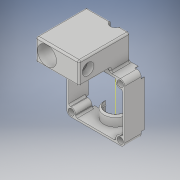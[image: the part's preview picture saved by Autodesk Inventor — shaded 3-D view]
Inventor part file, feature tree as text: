
AUTODESK INVENTOR PART (.ipt)
format: ipt  version: 2018 (Build 220112000, 112)  size: 484,864 bytes
history: native  units: mm
features: sketch x17, extrude x16, fillet x4, pattern_circular x3, mirror x2, other x1, revolve x1, chamfer x1
ambient origin geometry x8: Origin, YZ Plane, XZ Plane, XY Plane, X Axis, Y Axis, Z Axis, Center Point
bodies: Volumenkörper1 (feature_tree)
feature tree (45):
  extrude  "Extrusion1"  Depth=35.3mm
  extrude  "Extrusion2"  Depth=32.8mm
  extrude  "Extrusion3"  Depth=5.4mm
  extrude  "Extrusion4"  Depth=1.45mm
  extrude  "Extrusion5"  Depth=3.8mm
  pattern_circular  "Runde Anordnung1"  Count=4 Angle=360.0deg
  pattern_circular  "Runde Anordnung2"  Count=4 Angle=360.0deg
  fillet  "Rundung1"  Radius=2.7mm
  extrude  "Extrusion6"  Depth=17.65mm
  extrude  "Extrusion7"  Depth=14.2mm
  mirror  "Spiegeln1"
  sketch  "Skizze9"  dims[d16=12.0mm d17=0.0mm]
  other  "Arbeitsachse1"
  revolve  "Umdrehung1"
  mirror  "Spiegeln2"
  fillet  "Rundung2"  Radius=6.0mm
  chamfer  "Fase1"  Distance=1.0mm Angle=45.0deg
  extrude  "Extrusion8"  Depth=1.0mm
  extrude  "Extrusion9"  Depth=2.0mm TaperAngle=0.0deg
  pattern_circular  "Runde Anordnung3"  [2 undecoded]
  fillet  "Rundung3"  Radius=0.151856mm
  extrude  "Extrusion10"  Depth=1.0mm
  extrude  "Extrusion11"  Depth=1.0mm
  extrude  "Extrusion12"  Depth=2.0mm TaperAngle=0.0deg
  extrude  "Extrusion13"  Depth=1.0mm TaperAngle=360.0deg
  extrude  "Extrusion14"  Depth=1.0mm
  extrude  "Extrusion15"  Depth=1.0mm
  extrude  "Extrusion16"  Depth=1.0mm
  fillet  "Rundung4"  Radius=11.5mm
  sketch  "Skizze1"  dims[d0=35.3mm d1=35.3mm]
  sketch  "Skizze3"  dims[d2=32.8mm d3=32.8mm]
  sketch  "Skizze4"  dims[d4=12.0mm d5=0.0mm d6=5.4mm]
  sketch  "Skizze5"  dims[d7=3.8mm d9=1.45mm]
  sketch  "Skizze6"  dims[d10=12.0mm d11=0.0mm d12=3.8mm]
  sketch  "Skizze7"  dims[d13=12.0mm d14=0.0mm]
  sketch  "Skizze8"  dims[d15=1.45mm]
  sketch  "Skizze10"  dims[d18=1.45mm]
  sketch  "Skizze11"  dims[d19=12.0mm d20=0.0mm d21=40.0mm d22=360.0deg d24=40.0mm d25=360.0deg d27=2.7mm]
  sketch  "Skizze13"  dims[d28=12.0mm d29=17.65mm]
  sketch  "Skizze14"  dims[d30=12.0mm d31=0.0mm d32=14.2mm d33=6.0mm d34=0.0mm]
  sketch  "Skizze15"  dims[d35=0.25mm]
  sketch  "Skizze16"  dims[d36=0.8mm]
  sketch  "Skizze17"  dims[d37=4.5mm]
  sketch  "Skizze18"  dims[d38=180.0deg]
  sketch  "Skizze21"  dims[d39=0.45mm d40=1.0mm d41=2.0mm d42=45.0deg d43=5.4mm d44=2.0mm d45=0.0mm d46=0.253064mm d47=0.151856mm d48=0.263167mm d49=0.252607mm d51=2.0mm d52=0.0mm d53=40.0mm d54=360.0deg d56=1.0mm d57=26.5mm d58=15.5mm d59=11.5mm d60=7.0mm d61=8.75mm d62=31.0mm d63=0.0mm d64=6.2mm d65=12.0mm d66=0.0mm d67=2.0mm d68=0.0mm d69=3.0mm d70=7.0mm d71=5.25mm d72=3.1mm d73=29.0mm d74=0.0mm d75=7.0mm d76=4.1mm d77=4.0mm d78=0.0mm d79=4.1mm d80=15.5mm d81=0.0mm d84=25.5mm d85=2.0mm d86=19.0mm d87=0.0mm d88=1.0mm]
note: 2 required parameter values undecoded (feature->parameter linkage not recoverable at this tier; creation-order binding heuristic only, values carry confidence <= 0.55)
